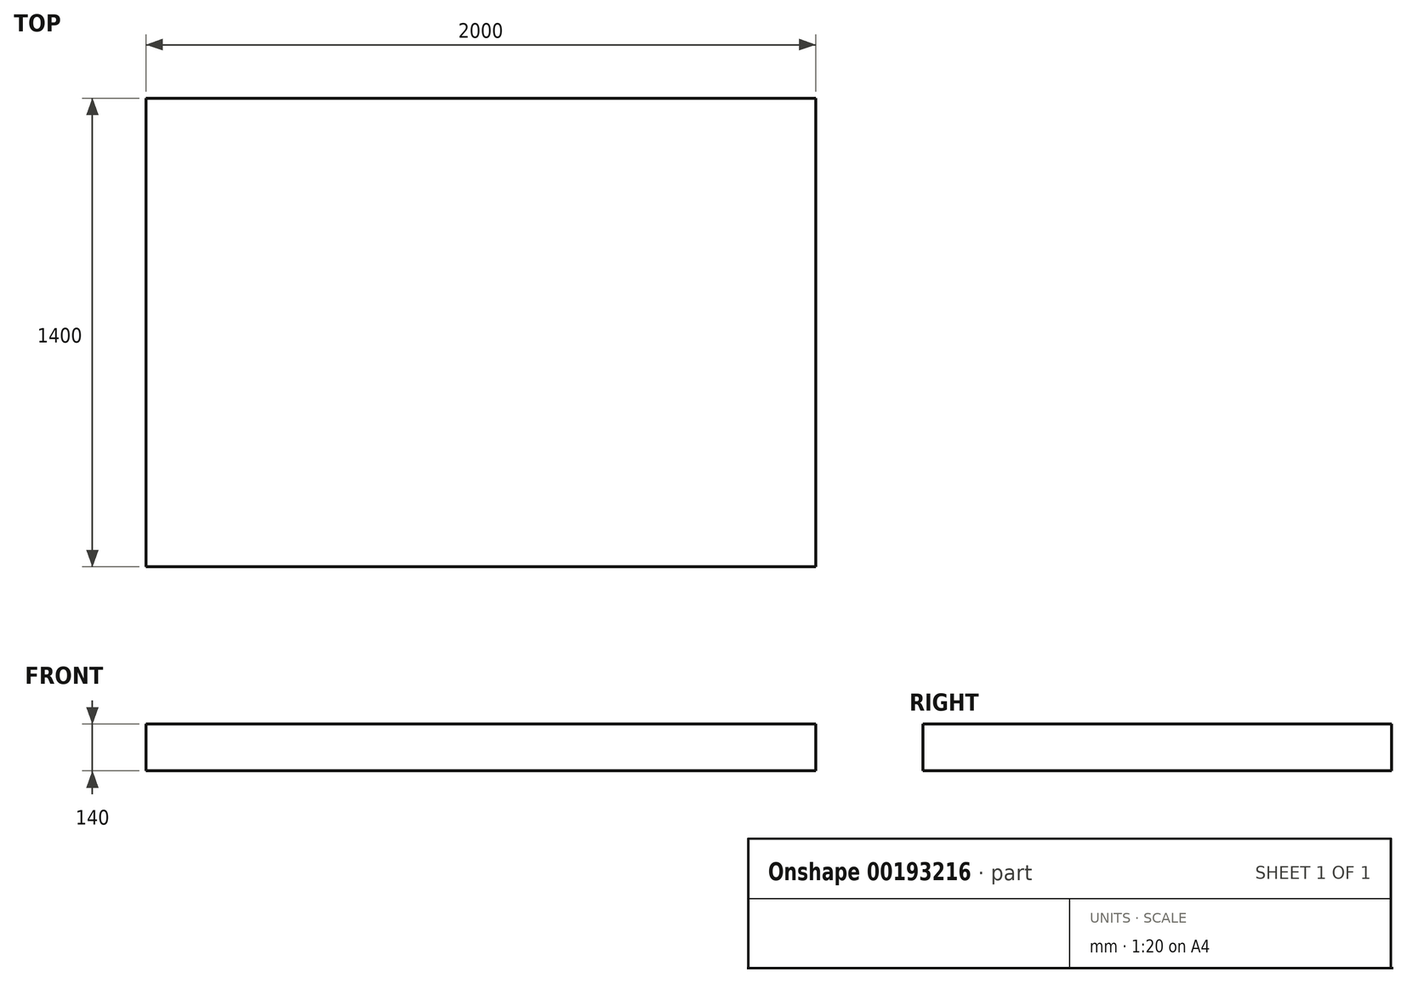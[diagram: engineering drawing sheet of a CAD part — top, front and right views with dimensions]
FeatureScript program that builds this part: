
annotation { "Feature Type Name" : "Feature", "Feature Type Description" : "" }
export const myFeature = defineFeature(function(context is Context, id is Id, definition is map)
    precondition{}
    {
        {
            var Q0;
            Q0=qCreatedBy(makeId("Top.planeOp"),FACE);
            var sketch = newSketch(context, id + "F0", { "sketchPlane" : qUnion([Q0])});
            skLineSegment(sketch, "E0.bottom", {"start": v(-2000, 1400) * mm, "end": v(0, 1400) * mm});
            skLineSegment(sketch, "E0.top", {"start": v(-2000, 0) * mm, "end": v(0, 0) * mm});
            skLineSegment(sketch, "E0.left", {"start": v(-2000, 1400) * mm, "end": v(-2000, 0) * mm});
            skLineSegment(sketch, "E0.right", {"start": v(0, 1400) * mm, "end": v(0, 0) * mm});
            skSolve(sketch);
        }
        {
            var Q0;
            Q0 = qSketchRegion(id + "F0", true);
            extrude(context, id + "F1", {"entities" : qUnion([Q0]), "depth" : 140 * mm});
        }
    });
